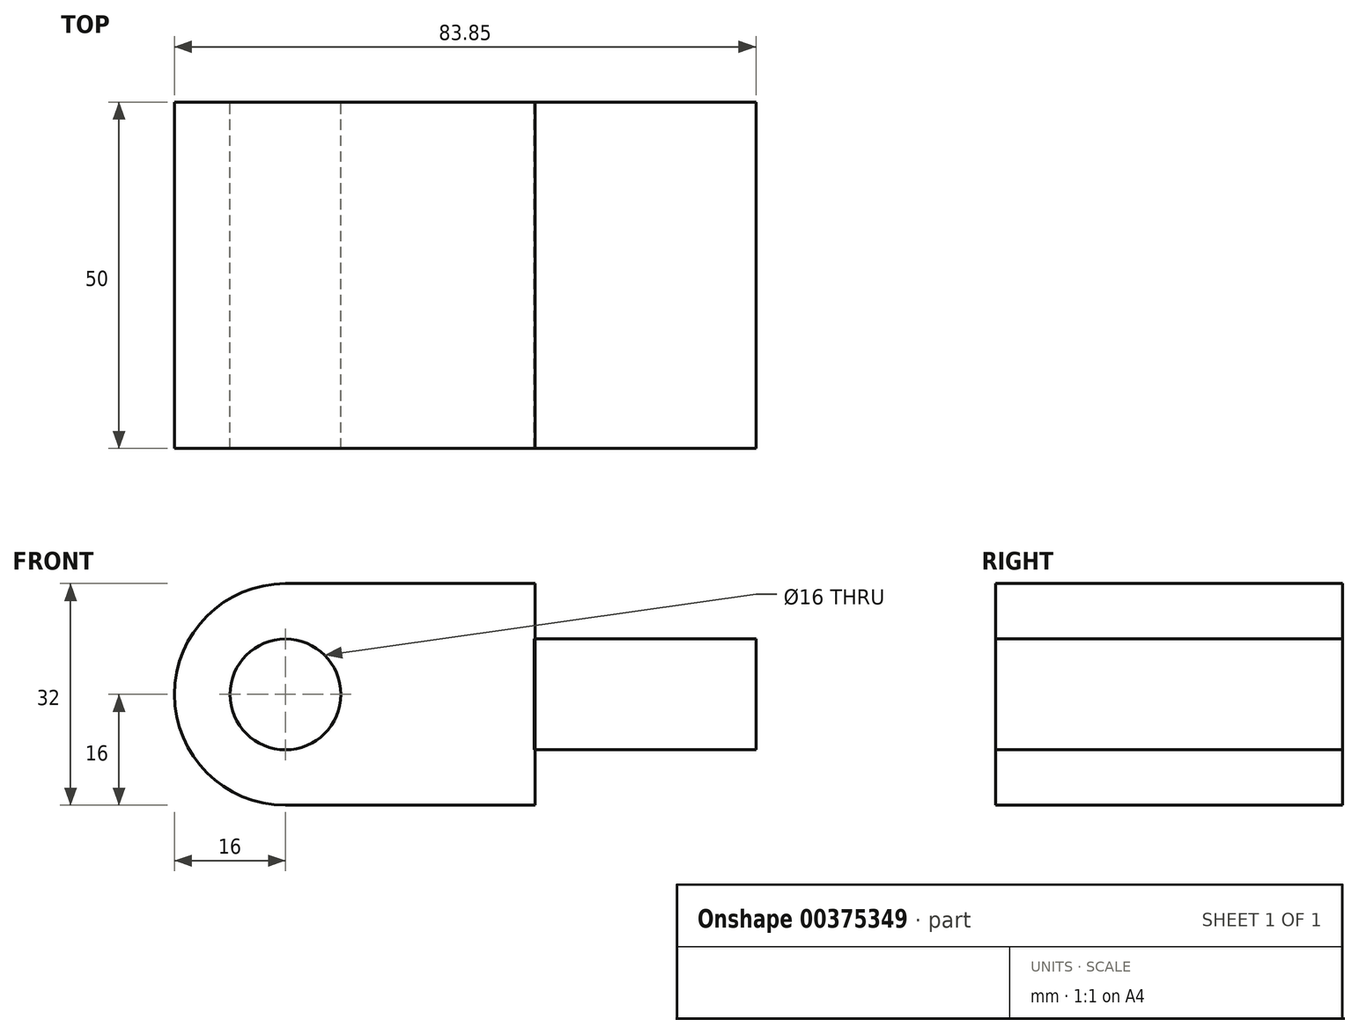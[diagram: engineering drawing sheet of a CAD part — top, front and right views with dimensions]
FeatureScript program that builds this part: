
annotation { "Feature Type Name" : "Feature", "Feature Type Description" : "" }
export const myFeature = defineFeature(function(context is Context, id is Id, definition is map)
    precondition{}
    {
        {
            var Q0;
            Q0=qCreatedBy(makeId("Front.planeOp"),FACE);
            var sketch = newSketch(context, id + "F0", { "sketchPlane" : qUnion([Q0])});
            skArc(sketch, "E0", {"start": v(0, 16) * mm, "mid": v(-16, 0) * mm, "end": v(0, -16) * mm});
            skLineSegment(sketch, "E1", {"start": v(0, 16) * mm, "end": v(36, 16) * mm});
            skLineSegment(sketch, "E2", {"start": v(0, -16) * mm, "end": v(36, -16) * mm});
            skLineSegment(sketch, "E3", {"start": v(36, 16) * mm, "end": v(36, -16) * mm});
            skCircle(sketch, "E4", {"center": v(0, 0) * mm, "radius": 8 * mm});
            skLineSegment(sketch, "E5.bottom", {"start": v(67.85, 8) * mm, "end": v(35.85, 8) * mm});
            skLineSegment(sketch, "E5.top", {"start": v(67.85, -8) * mm, "end": v(35.85, -8) * mm});
            skLineSegment(sketch, "E5.left", {"start": v(67.85, 8) * mm, "end": v(67.85, -8) * mm});
            skLineSegment(sketch, "E5.right", {"start": v(35.85, 8) * mm, "end": v(35.85, -8) * mm});
            skPoint(sketch, "E5.middle", {"position": v(51.85, 0) * mm});
            skSolve(sketch);
        }
        {
            var Q0;
            {var subQ5=sQuery(id+"F0.wireOp",EDGE,"E5.left");Q0=makeQuery(id+"F0.imprint","IMPRINT",FACE,{"disambiguationData":[TD([[makeQuery(id+"F0.imprint","IMPRINT",EDGE,{"derivedFrom":subQ5}),-1.0]])]});}
            var Q1;
            Q1=makeQuery(id+"F0.imprint","IMPRINT",FACE,{"disambiguationData":[TD([[makeQuery(id+"F0.imprint","IMPRINT",EDGE,{"derivedFrom":sQuery(id+"F0.wireOp",EDGE,"E0")}),1.0]])]});
            extrude(context, id + "F1", {"entities" : qUnion([Q0, Q1]), "depth" : 25 * mm});
        }
        {
            var Q0;
            Q0=makeQuery(id+"F1.opExtrude","SWEPT_BODY",BODY,{"disambiguationData":[OSD([sQuery(id+"F0.wireOp",EDGE,"E0"),sQuery(id+"F0.wireOp",EDGE,"E1"),sQuery(id+"F0.wireOp",EDGE,"E2"),sQuery(id+"F0.wireOp",EDGE,"E3"),sQuery(id+"F0.wireOp",EDGE,"E4"),sQuery(id+"F0.wireOp",EDGE,"E5.bottom"),sQuery(id+"F0.wireOp",EDGE,"E5.top"),sQuery(id+"F0.wireOp",EDGE,"E5.right")])]});
            var Q1;
            Q1=qCreatedBy(makeId("Front.planeOp"),FACE);
            mirror(context, id + "F2", {"operationType" : NewBodyOperationType.ADD, "entities" : qUnion([Q0]), "mirrorPlane" : qUnion([Q1])});
        }
        {
            var Q0;
            Q0=makeQuery(id+"F1.opExtrude","SWEPT_BODY",BODY,{"disambiguationData":[OSD([sQuery(id+"F0.wireOp",EDGE,"E3"),sQuery(id+"F0.wireOp",EDGE,"E5.bottom"),sQuery(id+"F0.wireOp",EDGE,"E5.top"),sQuery(id+"F0.wireOp",EDGE,"E5.left")])]});
            var Q1;
            Q1=qCreatedBy(makeId("Front.planeOp"),FACE);
            mirror(context, id + "F3", {"operationType" : NewBodyOperationType.ADD, "entities" : qUnion([Q0]), "mirrorPlane" : qUnion([Q1])});
        }
    });
